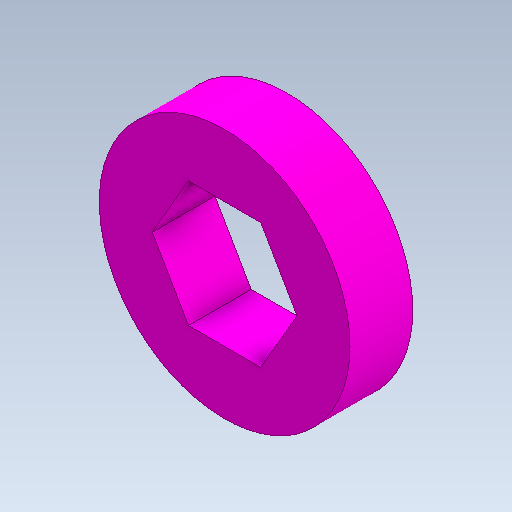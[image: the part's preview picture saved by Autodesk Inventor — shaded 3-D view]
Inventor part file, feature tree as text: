
AUTODESK INVENTOR PART (.ipt)
format: ipt  version: 2021.1 (Build 251245010, 245A)  size: 102,400 bytes
history: native  units: in
note: dims shown in document units (in); Inventor stores cm internally (conversion verified against a paired STEP export)
features: other x3, sketch x1
ambient origin geometry x8: Origin, YZ Plane, XZ Plane, XY Plane, X Axis, Y Axis, Z Axis, Center Point
bodies: Solid1 (feature_tree)
feature tree (4):
  other  "hexBearing.ipt"
  other  "Solid1::hexBearing.ipt"
  other  "TaggingFeature1"
  sketch  "Sketch1"  dims[d0=0.3937in]
